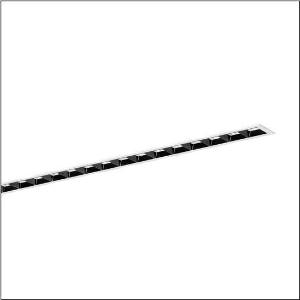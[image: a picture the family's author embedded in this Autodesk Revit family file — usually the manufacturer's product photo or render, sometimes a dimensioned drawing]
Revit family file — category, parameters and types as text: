
# Revit family: silica_r__21_51mx14da44wb_4ffe
name_source: partatom
category: Lighting Fixtures
units: mm (PartAtom-declared; Revit-internal decimal feet)

## family parameters
Cut with Voids When Loaded = No
Host = Face
Light Source = No
Part Type = Normal
Room Calculation Point = No
Round Connector Dimension = Use Diameter
Shared = No

## types (1)
- --- (1 x LED, 4320 lm, 30 W, 4000K)
    Apparent Load = 30 VA
    CIE Flux Codes = 74 94 99 100 100
    Color Rendering = 80
    Color Temperature = 4000K
    Default Elevation = 1800 mm
    Description = Silica® 21, office luminaire, primary light control with darklight reflector, of PMMA, black, light emission: direct distribution, primary light characteristic: asymmetric, installation type: recessed, LED, rated luminous flux: 4.320lm, luminous efficacy: 144lm/W, light colour: 840, colour temperature: 4000K, with terminal, 3+2-pole, max. 2.5mm², mains connection: 220..240V, AC, 50/60Hz, rated input power: 30W, luminaire housing, of aluminium, traffic white (RAL 9016), length: 1.228mm, width: 79mm, height: 53mm, protection rating (complete): IP20, insulation class (complete): insulation class I (protective earthing), certification: CE, permissible operating ambient temperature: 0..+35°C, standard: EN 50419, packaging unit: 1 piece
    Height = 0 mm  [stored 0 ft]
    Lamp = 1 x LED
    Lamp Light Flux = 4320 lm
    Lamp Power = 30 W
    Lamp count = 1
    Length = 1227 mm
    Luminous efficacy = 144 lm/W
    Manufacturer = Siteco
    ModVariant = No
    Model = 51MX14DA44WB
    Mounting Place = Ceiling
    Mounting Type = Recessed
    Number of Poles = 1
    OnlyDefault = Yes
    Power Factor = 1
    Product Name = Silica® 21
    Product group = office luminaire | ceiling recessed
    ProductGroupID = 401
    Protection Class = Protection class I
    Protection Degree = IP 20
    RLX_Detail_Level = 1
    RLX_Emergency_Light_Flux = 0 lm
    RLX_Emergency_Type = 0
    RLX_Emergency_Type_DB = No
    RlxData = <blob elided: 39313 chars, md5=c2251400>
    Socket = socket
    Standby Power = 0 W
    System Light Flux = 4320 lm
    System Power = 30 W
    Type Comments = factory setting: luminous flux: 100 % | dim-lin: 254 | 418 mA
    Type Image = l_1313610.jpg
    URL = http://relux.com
    VarID = @adj_071383
    Voltage = 0 V
    Weight = 0.00 kg
    Width = 79 mm

note: [stored X ft] marks values corroborated as IEEE doubles in the binary element streams (Revit-internal decimal feet)

## geometry (parser evidence)
native form markers: Blend x4, Sweep x10
no freeform markers — native parametric forms only
